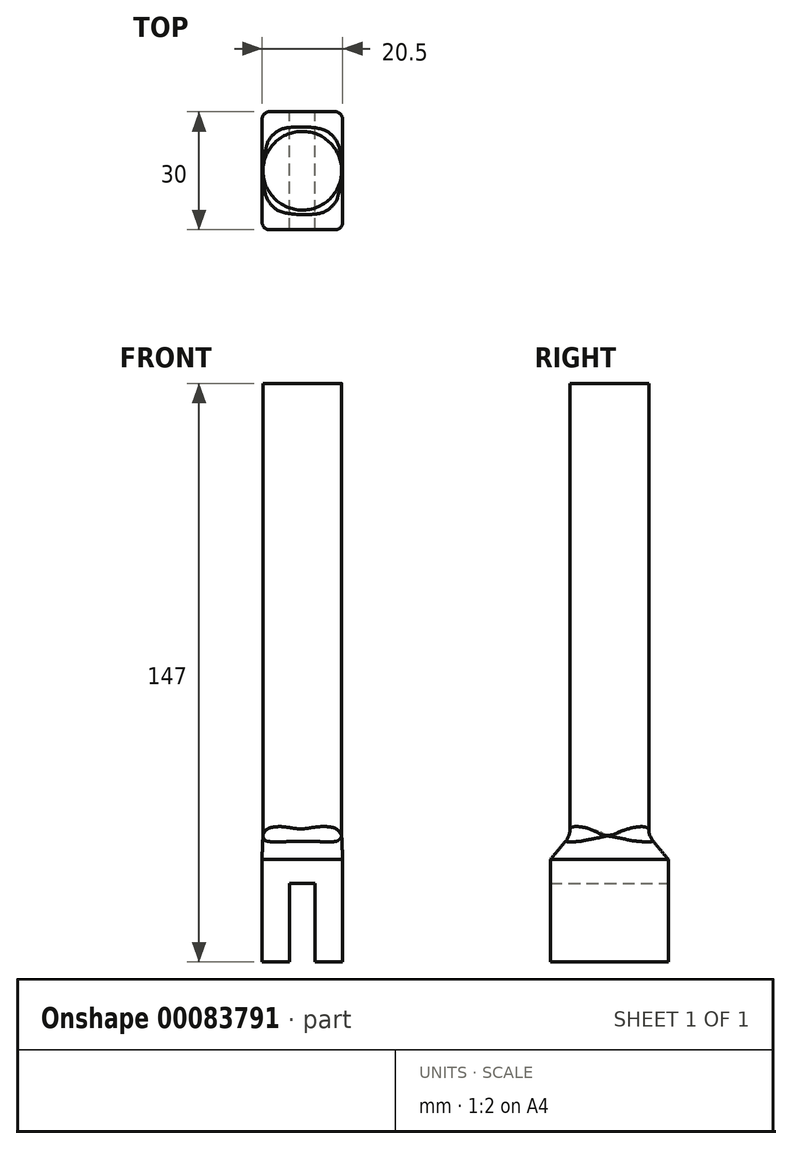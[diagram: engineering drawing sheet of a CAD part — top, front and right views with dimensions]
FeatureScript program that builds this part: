
annotation { "Feature Type Name" : "Feature", "Feature Type Description" : "" }
export const myFeature = defineFeature(function(context is Context, id is Id, definition is map)
    precondition{}
    {
        {
            var Q0;
            Q0=qCreatedBy(makeId("Front.planeOp"),FACE);
            var sketch = newSketch(context, id + "F0", { "sketchPlane" : qUnion([Q0])});
            skLineSegment(sketch, "E0", {"start": v(-10.25, -20) * mm, "end": v(-3.25, -20) * mm});
            skLineSegment(sketch, "E1", {"start": v(-3.25, -20) * mm, "end": v(-3.25, 0) * mm});
            skLineSegment(sketch, "E2", {"start": v(-3.25, 0) * mm, "end": v(3.25, 0) * mm});
            skLineSegment(sketch, "E3", {"start": v(3.25, 0) * mm, "end": v(3.25, -20) * mm});
            skLineSegment(sketch, "E4", {"start": v(3.25, -20) * mm, "end": v(10.25, -20) * mm});
            skLineSegment(sketch, "E5", {"start": v(10.25, -20) * mm, "end": v(10.25, 6) * mm});
            skLineSegment(sketch, "E6", {"start": v(10.25, 6) * mm, "end": v(-10.25, 6) * mm});
            skLineSegment(sketch, "E7", {"start": v(-10.25, 6) * mm, "end": v(-10.25, -20) * mm});
            skSolve(sketch);
        }
        {
            var Q0;
            Q0=makeQuery(id+"F0.imprint","IMPRINT",FACE,{"disambiguationData":[TD([[makeQuery(id+"F0.imprint","IMPRINT",EDGE,{"derivedFrom":sQuery(id+"F0.wireOp",EDGE,"E0")}),1.0]])]});
            extrude(context, id + "F1", {"entities" : qUnion([Q0]), "endBound" : BoundingType.SYMMETRIC, "depth" : 30 * mm});
        }
        {
            var Q0;
            Q0=makeQuery(id+"F1.opExtrude","CAP_EDGE",EDGE,{"disambiguationData":[OSD([sQuery(id+"F0.wireOp",EDGE,"E5")])],"isStart":false});
            var Q1;
            Q1=makeQuery(id+"F1.opExtrude","CAP_EDGE",EDGE,{"disambiguationData":[OSD([sQuery(id+"F0.wireOp",EDGE,"E5")])],"isStart":true});
            var Q2;
            Q2=makeQuery(id+"F1.opExtrude","CAP_EDGE",EDGE,{"disambiguationData":[OSD([sQuery(id+"F0.wireOp",EDGE,"E7")])],"isStart":false});
            var Q3;
            Q3=makeQuery(id+"F1.opExtrude","CAP_EDGE",EDGE,{"disambiguationData":[OSD([sQuery(id+"F0.wireOp",EDGE,"E7")])],"isStart":true});
            fillet(context, id + "F2", {"entities" : qUnion([Q0, Q1, Q2, Q3]), "radius" : 2 * mm, "tangentPropagation" : true, "allowEdgeOverflow" : false});
        }
        {
            var Q0;
            Q0=makeQuery(id+"F1.opExtrude","CAP_FACE",FACE,{"disambiguationData":[OSD([sQuery(id+"F0.wireOp",EDGE,"E0"),sQuery(id+"F0.wireOp",EDGE,"E1"),sQuery(id+"F0.wireOp",EDGE,"E2"),sQuery(id+"F0.wireOp",EDGE,"E3"),sQuery(id+"F0.wireOp",EDGE,"E4"),sQuery(id+"F0.wireOp",EDGE,"E5"),sQuery(id+"F0.wireOp",EDGE,"E6"),sQuery(id+"F0.wireOp",EDGE,"E7")])],"isStart":false});
            var sketch = newSketch(context, id + "F3", { "sketchPlane" : qUnion([Q0])});
            skLineSegment(sketch, "E8.bottom", {"start": v(-10, 6) * mm, "end": v(10, 6) * mm});
            skLineSegment(sketch, "E8.top", {"start": v(-10, 12) * mm, "end": v(10, 12) * mm});
            skLineSegment(sketch, "E8.left", {"start": v(-10, 6) * mm, "end": v(-10, 12) * mm});
            skLineSegment(sketch, "E8.right", {"start": v(10, 6) * mm, "end": v(10, 12) * mm});
            skSolve(sketch);
        }
        {
            var Q0;
            Q0 = qSketchRegion(id + "F3", true);
            extrude(context, id + "F4", {"entities" : qUnion([Q0]), "operationType" : NewBodyOperationType.ADD, "depth" : 40 * mm});
        }
        {
            var Q0;
            Q0=makeQuery(id+"F4.opExtrude","SWEPT_FACE",FACE,{"disambiguationData":[OSD([sQuery(id+"F3.wireOp",EDGE,"E8.top")])]});
            var sketch = newSketch(context, id + "F5", { "sketchPlane" : qUnion([Q0])});
            skCircle(sketch, "E9", {"center": v(0, 0) * mm, "radius": 10 * mm});
            skSolve(sketch);
        }
        {
            var Q0;
            Q0=makeQuery(id+"F1.opExtrude","SWEPT_FACE",FACE,{"disambiguationData":[OSD([sQuery(id+"F0.wireOp",EDGE,"E6")])]});
            var Q1;
            Q1 = qSketchRegion(id + "F5", true);
            loft(context, id + "F6", {"sheetProfilesArray" : [{ "sheetProfileEntities" : qUnion([Q0]) }, { "sheetProfileEntities" : qUnion([Q1]) }]});
        }
        {
            var Q0;
            Q0=makeQuery(id+"F4.opExtrude","SWEPT_BODY",BODY,{"disambiguationData":[OSD([sQuery(id+"F3.wireOp",EDGE,"E8.bottom"),sQuery(id+"F3.wireOp",EDGE,"E8.top"),sQuery(id+"F3.wireOp",EDGE,"E8.left"),sQuery(id+"F3.wireOp",EDGE,"E8.right")])]});
            deleteBodies(context, id + "F7", {"entities" : qUnion([Q0])});
        }
        {
            var Q0;
            Q0=makeQuery(id+"F6.opLoft","CAP_FACE",FACE,{"disambiguationData":[OSD([makeQuery(id+"F5.imprint","IMPRINT",FACE,{"disambiguationData":[TD([[makeQuery(id+"F5.imprint","IMPRINT",EDGE,{"derivedFrom":sQuery(id+"F5.wireOp",EDGE,"E9")}),1.0]])]})])],"isStart":true});
            extrude(context, id + "F8", {"entities" : qUnion([Q0]), "operationType" : NewBodyOperationType.ADD, "depth" : 115 * mm});
        }
        {
            var Q0;
            {var subQ0=sQuery(id+"F5.wireOp",EDGE,"E9");var subQ1=sQuery(id+"F0.wireOp",EDGE,"E6");var subQ2=makeQuery(id+"F1.opExtrude","SWEPT_FACE",FACE,{"disambiguationData":[OSD([subQ1])]});var subQ3=sQuery(id+"F0.wireOp",EDGE,"E5");var subQ4=makeQuery(id+"F1.opExtrude","CAP_EDGE",EDGE,{"disambiguationData":[OSD([subQ3])],"isStart":false});var subQ5=sQuery(id+"F0.wireOp",EDGE,"E7");var subQ6=sQuery(id+"F0.wireOp",EDGE,"E4");var subQ7=sQuery(id+"F0.wireOp",EDGE,"E3");var subQ8=sQuery(id+"F0.wireOp",EDGE,"E2");var subQ9=sQuery(id+"F0.wireOp",EDGE,"E1");var subQ10=sQuery(id+"F0.wireOp",EDGE,"E0");var subQ11=makeQuery(id+"F6.opLoft","MID_CAP_EDGE",EDGE,{"disambiguationData":[OSD([subQ10,subQ9,subQ8,subQ7,subQ6,subQ3,subQ1,subQ5,subQ0]),TDD([makeQuery(id+"F2.opFillet","BLEND_VERTEX",VERTEX,{"blendedFrom":[subQ4,makeQuery(id+"F1.opExtrude","CAP_FACE",FACE,{"disambiguationData":[OSD([subQ10,subQ9,subQ8,subQ7,subQ6,subQ3,subQ1,subQ5])],"isStart":false}),subQ2],"blendedInto":[makeQuery(id+"F1.opExtrude","CAP_FACE",FACE,{"disambiguationData":[OSD([subQ10,subQ9,subQ8,subQ7,subQ6,subQ3,subQ1,subQ5])],"isStart":false}),subQ2]}),makeQuery(id+"F2.opFillet","BLEND_VERTEX",VERTEX,{"blendedFrom":[subQ4,makeQuery(id+"F1.opExtrude","SWEPT_FACE",FACE,{"disambiguationData":[OSD([subQ3])]}),subQ2],"blendedInto":[makeQuery(id+"F1.opExtrude","SWEPT_FACE",FACE,{"disambiguationData":[OSD([subQ3])]}),subQ2]}),makeQuery(id+"F5.imprint","IMPRINT",EDGE,{"derivedFrom":subQ0})])],"capPos":1.0});Q0=makeQuery(id+"F8.boolean.opBoolean","MERGE",EDGE,{"derivedFrom":[subQ11,makeQuery(id+"F8.opExtrude","CAP_EDGE",EDGE,{"disambiguationData":[OSD([subQ10,subQ9,subQ8,subQ7,subQ6,subQ3,subQ1,subQ5,subQ0]),TDD([subQ11])],"isStart":true})]});}
            var Q1;
            {var subQ0=sQuery(id+"F5.wireOp",EDGE,"E9");var subQ1=sQuery(id+"F0.wireOp",EDGE,"E6");var subQ2=makeQuery(id+"F1.opExtrude","SWEPT_FACE",FACE,{"disambiguationData":[OSD([subQ1])]});var subQ3=sQuery(id+"F0.wireOp",EDGE,"E5");var subQ4=sQuery(id+"F0.wireOp",EDGE,"E7");var subQ5=sQuery(id+"F0.wireOp",EDGE,"E4");var subQ6=sQuery(id+"F0.wireOp",EDGE,"E3");var subQ7=sQuery(id+"F0.wireOp",EDGE,"E2");var subQ8=sQuery(id+"F0.wireOp",EDGE,"E1");var subQ9=sQuery(id+"F0.wireOp",EDGE,"E0");var subQ10=makeQuery(id+"F6.opLoft","MID_CAP_EDGE",EDGE,{"disambiguationData":[OSD([subQ9,subQ8,subQ7,subQ6,subQ5,subQ3,subQ1,subQ4,subQ0]),TDD([makeQuery(id+"F2.opFillet","BLEND_VERTEX",VERTEX,{"blendedFrom":[makeQuery(id+"F1.opExtrude","CAP_EDGE",EDGE,{"disambiguationData":[OSD([subQ3])],"isStart":true}),makeQuery(id+"F1.opExtrude","CAP_FACE",FACE,{"disambiguationData":[OSD([subQ9,subQ8,subQ7,subQ6,subQ5,subQ3,subQ1,subQ4])],"isStart":true}),subQ2],"blendedInto":[makeQuery(id+"F1.opExtrude","CAP_FACE",FACE,{"disambiguationData":[OSD([subQ9,subQ8,subQ7,subQ6,subQ5,subQ3,subQ1,subQ4])],"isStart":true}),subQ2]}),makeQuery(id+"F2.opFillet","BLEND_VERTEX",VERTEX,{"blendedFrom":[makeQuery(id+"F1.opExtrude","CAP_EDGE",EDGE,{"disambiguationData":[OSD([subQ3])],"isStart":false}),makeQuery(id+"F1.opExtrude","SWEPT_FACE",FACE,{"disambiguationData":[OSD([subQ3])]}),subQ2],"blendedInto":[makeQuery(id+"F1.opExtrude","SWEPT_FACE",FACE,{"disambiguationData":[OSD([subQ3])]}),subQ2]}),makeQuery(id+"F5.imprint","IMPRINT",EDGE,{"derivedFrom":subQ0})])],"capPos":1.0});Q1=makeQuery(id+"F8.boolean.opBoolean","MERGE",EDGE,{"derivedFrom":[subQ10,makeQuery(id+"F8.opExtrude","CAP_EDGE",EDGE,{"disambiguationData":[OSD([subQ9,subQ8,subQ7,subQ6,subQ5,subQ3,subQ1,subQ4,subQ0]),TDD([subQ10])],"isStart":true})]});}
            fillet(context, id + "F9", {"entities" : qUnion([Q0, Q1]), "radius" : 5 * mm, "tangentPropagation" : true, "allowEdgeOverflow" : false});
        }
    });
